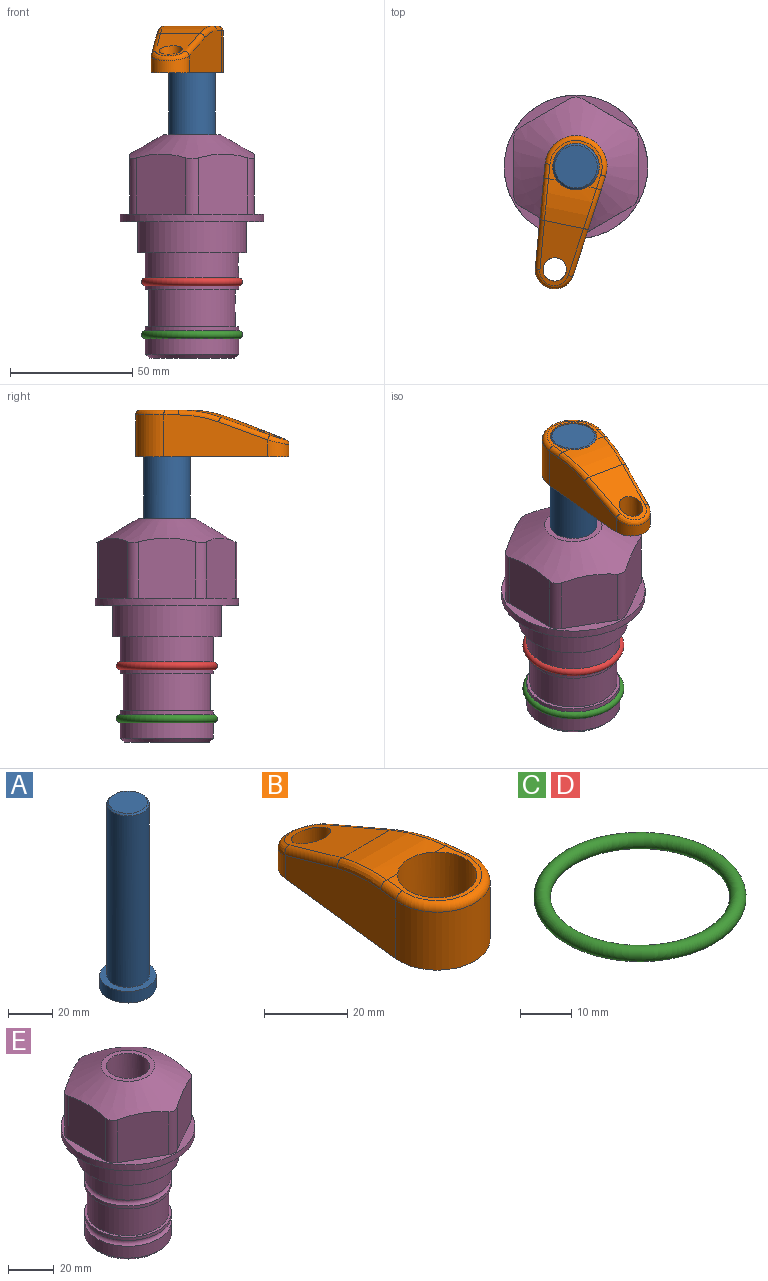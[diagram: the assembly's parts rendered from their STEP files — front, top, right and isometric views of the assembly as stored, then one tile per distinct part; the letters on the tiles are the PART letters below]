
ASSEMBLY  parts=5 mates=3
PART A: 6 faces, bbox 25.4x25.4x101.6 mm
  f0: plane 17.46x17.46mm, normal (0,0,1), area 239.5mm2, adj f5
  f1: plane 25.4x25.4mm, normal (0,0,-1), area 506.7mm2, adj f2
  f2: cylinder r=12.7mm len=25.4mm, axis (0,0,1), area 506.7mm2, adj f1,f3
  f3: plane 25.4x25.4mm, normal (0,0,1), area 221.7mm2, adj f2,f4
  f4: cylinder r=9.53mm len=94.46mm, axis (0,0,1), area 5653mm2, adj f3,f5
  f5: cone r=8.73mm half-angle=45deg, axis (0,0,-1), area 64.4mm2, adj f0,f4
PART B: 28 faces, bbox 27.5x64.6x19.1 mm
  f0: plane 63.5x25.4mm, normal (0,0,-1), area 561.7mm2, adj f1,f2,f3,f4,f5,f6,f18,f19
  f1: cylinder r=12.7mm len=25.4mm, axis (0,0,-1), area 728.5mm2, adj f0,f2,f4,f12
  f2: plane 42.33x17.05mm, normal (0.99,0.11,0), area 578.6mm2, adj f0,f1,f3,f10,f11,f13
  f3: cylinder r=7.94mm len=15.78mm, axis (0,0,-1), area 130.4mm2, adj f0,f2,f4,f15
  f4: plane 42.33x17.05mm, normal (-0.99,0.11,0), area 578.6mm2, adj f0,f1,f3,f14,f16,f17
  f5: cylinder r=9.53mm len=19.05mm, axis (0,0,-1), area 1140.1mm2, adj f0,f7,f9
  f6: cylinder r=4.76mm len=10.98mm, axis (0,0,-1), area 276.1mm2, adj f0,f8
  f7: plane 21.4x17.76mm, normal (0,0,1), area 62.8mm2, adj f5,f9,f10,f12,f14
  f8: plane 25.32x16.28mm, normal (0,0.34,0.94), area 274.4mm2, adj f6,f9,f13,f15,f17
  f9: cylinder r=50mm len=19.96mm, axis (-1,0,0), area 294.6mm2, adj f5,f7,f8,f11,f16
  f10: cylinder r=2mm len=6.09mm, axis (0.11,-0.99,0), area 18.6mm2, adj f2,f7,f11,f12
  f11: bspline ~17.13x4.89mm, area 53.7mm2, adj f2,f9,f10,f13
  f12: torus R=10.7mm, axis (0,0,1), area 126.5mm2, adj f1,f7,f10,f14
  f13: cylinder r=2mm len=20.54mm, axis (0.1,-0.93,0.34), area 65.8mm2, adj f2,f8,f11,f15
  f14: cylinder r=2mm len=6.09mm, axis (0.11,0.99,0), area 18.6mm2, adj f4,f7,f12,f16
  f15: bspline ~15.78x7.05mm, area 56.7mm2, adj f3,f8,f13,f17
  f16: bspline ~17.13x4.89mm, area 53.7mm2, adj f4,f9,f14,f17
  f17: cylinder r=2mm len=20.54mm, axis (0.1,0.93,-0.34), area 65.8mm2, adj f4,f8,f15,f16
  f18: plane 21.62x15.53mm, normal (-0.99,-0.11,0), area 274.7mm2, adj f0,f22,f23,f24,f26
  f19: plane 21.62x15.53mm, normal (0.99,-0.11,0), area 274.7mm2, adj f0,f22,f23,f25,f27
  f20: cylinder r=12.7mm len=15.68mm, axis (0,0,-1), area 189.1mm2, adj f0,f23,f24,f25
  f21: cylinder r=7.94mm len=8.74mm, axis (0,0,-1), area 61.9mm2, adj f0,f22,f26,f27
  f22: plane 14.01x12.8mm, normal (0,-0.34,-0.94), area 165.3mm2, adj f18,f19,f21,f23,f26,f27
  f23: cylinder r=46.82mm len=16.31mm, axis (-1,0,0), area 173.9mm2, adj f18,f19,f20,f22,f24,f25
  f24: cylinder r=1.59mm len=15.68mm, axis (0,0,-1), area 53.5mm2, adj f0,f18,f20,f23
  f25: cylinder r=1.59mm len=15.68mm, axis (0,0,-1), area 53.5mm2, adj f0,f19,f20,f23
  f26: cylinder r=1.59mm len=8.9mm, axis (0,0,-1), area 25.9mm2, adj f0,f18,f21,f22
  f27: cylinder r=1.59mm len=8.9mm, axis (0,0,-1), area 25.9mm2, adj f0,f19,f21,f22
PART C: 1 faces, bbox 44.7x44.7x3.2 mm
  f0: torus R=19.05mm, axis (0,0,1), area 1193.9mm2
PART D: same geometry as C
PART E: 36 faces, bbox 58.7x58.7x91.2 mm
  f0: cylinder r=17.78mm len=35.56mm, axis (0,0,1), area 1670.8mm2, adj f23,f24,f31
  f1: cylinder r=19.05mm len=38.1mm, axis (0,0,1), area 1191.9mm2, adj f26,f27,f30
  f2: plane 58.66x58.66mm, normal (0,0,-1), area 1150.6mm2, adj f3,f28
  f3: cylinder r=29.33mm len=58.66mm, axis (0,0,-1), area 585.1mm2, adj f2,f4
  f4: plane 58.66x58.66mm, normal (0,0,1), area 475.9mm2, adj f3,f5,f6,f7,f8,f9,f10,f11
  f5: plane 24.5x20.32mm, normal (-0.5,0.87,0), area 562.8mm2, adj f4,f15,f16,f17
  f6: plane 24.5x20.32mm, normal (0.5,0.87,0), area 562.8mm2, adj f4,f14,f15,f17
  f7: plane 24.5x23.48mm, normal (1,0,0), area 562.8mm2, adj f4,f13,f14,f17
  f8: plane 24.5x20.32mm, normal (0.5,-0.87,0), area 562.8mm2, adj f4,f12,f13,f17
  f9: plane 24.5x20.32mm, normal (-0.5,-0.87,0), area 562.8mm2, adj f4,f11,f12,f17
  f10: plane 24.5x23.48mm, normal (-1,0,0), area 562.8mm2, adj f4,f11,f16,f17
  f11: cylinder r=5.08mm len=23.01mm, axis (0,0,-1), area 121.2mm2, adj f4,f9,f10,f17
  f12: cylinder r=5.08mm len=23.01mm, axis (0,0,-1), area 121.2mm2, adj f4,f8,f9,f17
  f13: cylinder r=5.08mm len=23.01mm, axis (0,0,-1), area 121.2mm2, adj f4,f7,f8,f17
  f14: cylinder r=5.08mm len=23.01mm, axis (0,0,-1), area 121.2mm2, adj f4,f6,f7,f17
  f15: cylinder r=5.08mm len=23.01mm, axis (0,0,-1), area 121.2mm2, adj f4,f5,f6,f17
  f16: cylinder r=5.08mm len=23.01mm, axis (0,0,-1), area 121.2mm2, adj f4,f5,f10,f17
  f17: cone r=11.73mm half-angle=60deg, axis (0,0,-1), area 2071.8mm2, adj f5,f6,f7,f8,f9,f10,f11,f12
  f18: plane 23.46x23.46mm, normal (0,0,1), area 147.4mm2, adj f17,f35
  f19: plane 34.93x34.93mm, normal (0,0,-1), area 958mm2, adj f29
  f20: cylinder r=19.05mm len=38.1mm, axis (0,0,1), area 760.1mm2, adj f21,f29
  f21: torus R=19.05mm, axis (0,0,1), area 565.3mm2, adj f20,f22
  f22: cylinder r=19.05mm len=38.1mm, axis (0,0,1), area 190mm2, adj f21,f23
  f23: plane 38.1x38.1mm, normal (0,0,1), area 146.9mm2, adj f0,f22
  f24: plane 38.1x38.1mm, normal (0,0,-1), area 146.9mm2, adj f0,f25
  f25: cylinder r=19.05mm len=38.1mm, axis (0,0,1), area 190mm2, adj f24,f26
  f26: torus R=19.05mm, axis (0,0,1), area 565.3mm2, adj f1,f25
  f27: plane 44.45x44.45mm, normal (0,0,-1), area 411.7mm2, adj f1,f28
  f28: cylinder r=22.23mm len=44.45mm, axis (0,0,1), area 1773.5mm2, adj f2,f27
  f29: cone r=19.05mm half-angle=45deg, axis (0,0,1), area 257.5mm2, adj f19,f20
  f30: cylinder r=3.17mm len=6.75mm, axis (-1,0,0), area 128mm2, adj f1,f33
  f31: cylinder r=3.17mm len=6.35mm, axis (-1,0,0), area 102.5mm2, adj f0,f33
  f32: plane 25.4x25.4mm, normal (0,0,1), area 506.7mm2, adj f33
  f33: cylinder r=12.7mm len=66.42mm, axis (0,0,-1), area 5236.2mm2, adj f30,f31,f32,f34
  f34: cone r=9.53mm half-angle=30deg, axis (0,0,-1), area 443.4mm2, adj f33,f35
  f35: cylinder r=9.53mm len=19.05mm, axis (0,0,-1), area 849mm2, adj f18,f34
PLACE A rot(axis=(0,0,-1),101.7deg) t=(0,0,6.38)mm
PLACE B rot(axis=(0,0,1),168.3deg) t=(0,0,60.99)mm
PLACE C t=(0,0,-21.59)mm
PLACE D at identity
PLACE E at identity fixed
MATE fastened C.f0 <-> E.f0  axis (0,0,1) through (0,0,-46.1)mm
MATE cylindrical A.f2 <-> E.f0  axis (0,0,1) through (0,0,32.01)mm
MATE fastened B.f1 <-> A.f2  axis (0,0,1) through (0,0,80.04)mm
